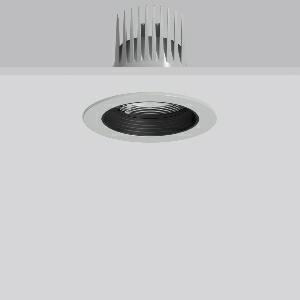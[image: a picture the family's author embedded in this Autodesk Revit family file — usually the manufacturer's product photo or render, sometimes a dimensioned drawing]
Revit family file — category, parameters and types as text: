
# Revit family: heledon_maxi_e_901769_004_1_7216
name_source: partatom
category: Lighting Fixtures
units: mm (PartAtom-declared; Revit-internal decimal feet)

## family parameters
Cut with Voids When Loaded = No
Host = Face
Light Source = No
Part Type = Normal
Room Calculation Point = No
Round Connector Dimension = Use Diameter
Shared = No

## types (1)
- HELEDON maxi E (1 x LED Modul 940, 3800 lm, 4000)
    Apparent Load = 35 VA
    Approval mark = CE
    CIE Flux Codes = 96 100 100 100 100
    Color Rendering = 92
    Color Temperature = 4000
    Default Elevation = 1800 mm
    Description = Series: HELEDON maxi
Round recessed downlight. Housing: die-cast aluminium, powder-coated. Black plastic ring and recessed LED to prevent glare from the side. Optical assembly with lens made of plastic (polycarbonate) for the best homogeneous light distribution - can be changed without tools. Best colour rendering index Ra>90. Suitable for Recessed ceiling mounting. Installation without tools thanks to spring fastening system. Including separate LED converter with connecting cable 600 mm.High quality converter without flickering and stroboscopic effect. Through-wiring box (5 pole) available as accessory. The following accessories can be mounted without use of tools: interchangeable lenses, decorative glasses, honeycomb louvre, clear and frosted diffusers, white interchangeable plastic ring. 
Colour: silver
Diameter: 162 mm
Height: 3 mm
Cut-out diameter: 152 mm
Recess height: 200 mm
Luminaire: recess height: 135 mm
Lamp: LED
Socket: without socket
Colour temperature: 4000K
Colour rendering index (CRI): 92
System power: 35 W
Rated luminous flux: 3800 lm
Luminous efficiency: 109 lm/W
Control gear: Regulated power supply
Protection class: II
Type of protection: IP 20
    Height = 0 mm  [stored 0 ft]
    Lamp = 1 x LED Modul 940
    Lamp Light Flux = 3800 lm
    Lamp count = 1
    Length = 162 mm
    Lifetime = 50000 h
    Luminous efficacy = 109 lm/W
    Manufacturer = RZB
    ModVariant = No
    Model = 901769.004.1
    Mounting Place = Ceiling
    Mounting Type = Recessed
    Number of Poles = 1
    OnlyDefault = Yes
    Power Factor = 1
    Product Name = HELEDON maxi E
    Product group = Recessed downlights
    ProductGroupID = 402
    Protection Class = Protection class II
    Protection Degree = IP 20
    RLX_Detail_Level = 1
    RLX_Emergency_Light_Flux = 0 lm
    RLX_Emergency_Type = 0
    RLX_Emergency_Type_DB = No
    RlxData = <blob elided: 119233 chars, md5=e7c73ff7>
    Socket = socket
    Standby Power = 0 W
    System Light Flux = 3800 lm
    System Power = 35 W
    Type Comments = Product without accessories
    Type Image = 901663.004.jpg
    URL = http://relux.com
    VarID = ---
    Voltage = 230 V
    Voltage Range = 220-240 V
    Weight = 0.00 kg
    Width = 0 mm  [stored 0 ft]

note: [stored X ft] marks values corroborated as IEEE doubles in the binary element streams (Revit-internal decimal feet)

## geometry (parser evidence)
native form markers: Blend x4, Sweep x12
no freeform markers — native parametric forms only
